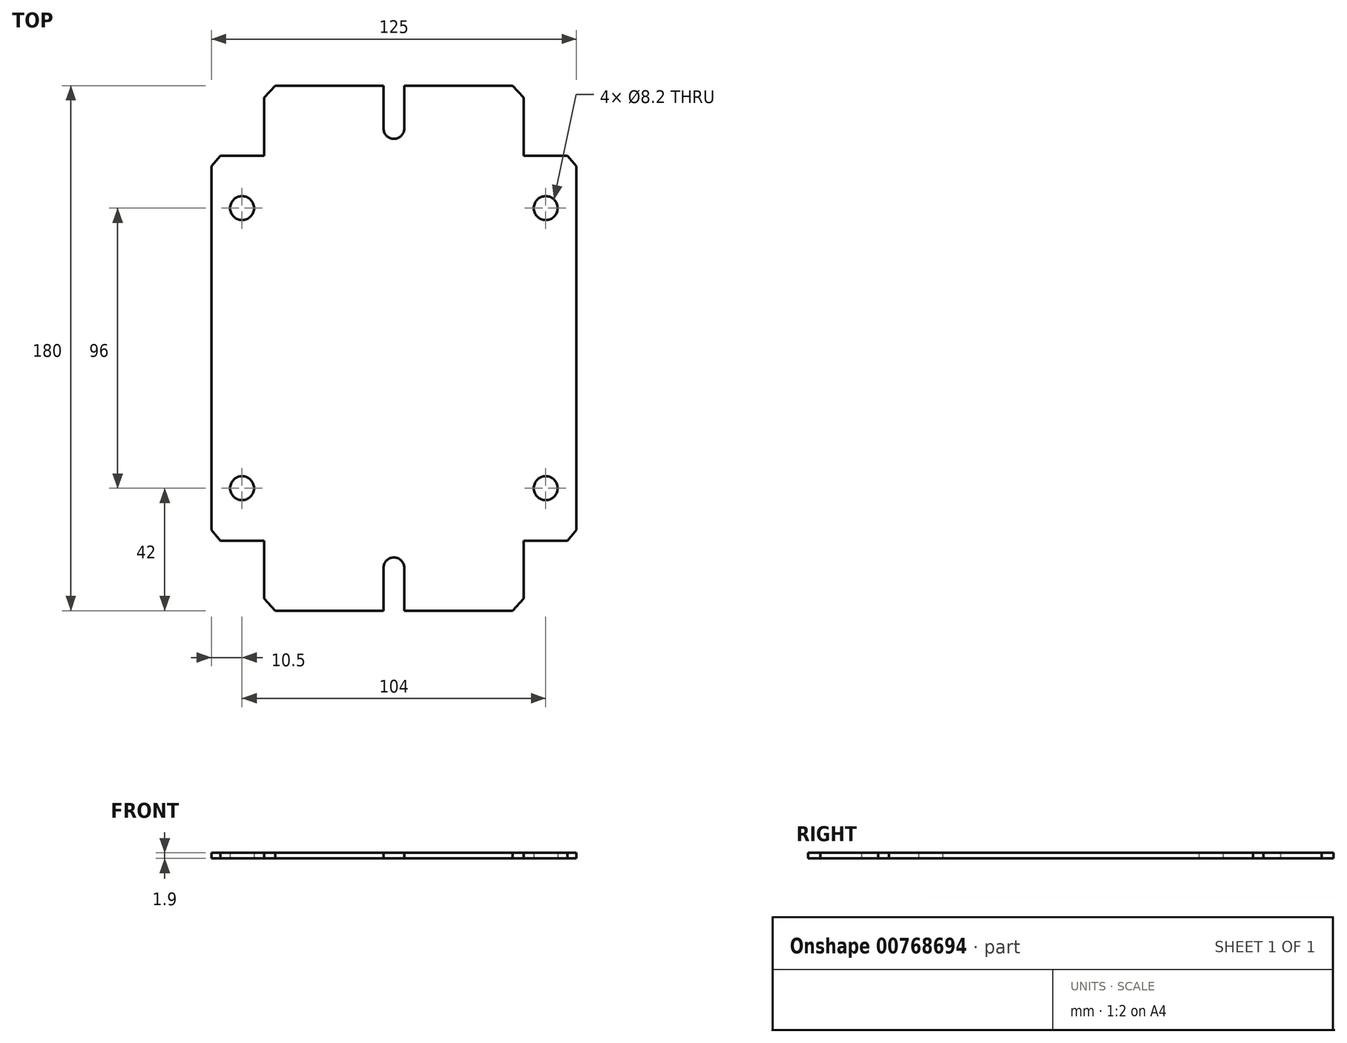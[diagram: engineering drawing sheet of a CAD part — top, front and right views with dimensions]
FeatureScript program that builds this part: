
annotation { "Feature Type Name" : "Feature", "Feature Type Description" : "" }
export const myFeature = defineFeature(function(context is Context, id is Id, definition is map)
    precondition{}
    {
        {
            var Q0;
            Q0=qCreatedBy(makeId("Top.planeOp"),FACE);
            var sketch = newSketch(context, id + "F0", { "sketchPlane" : qUnion([Q0])});
            skLineSegment(sketch, "E0.bottom", {"start": v(62.5, -90) * mm, "end": v(-62.5, -90) * mm});
            skLineSegment(sketch, "E0.top", {"start": v(62.5, 90) * mm, "end": v(-62.5, 90) * mm});
            skLineSegment(sketch, "E0.left", {"start": v(62.5, -90) * mm, "end": v(62.5, 90) * mm});
            skLineSegment(sketch, "E0.right", {"start": v(-62.5, -90) * mm, "end": v(-62.5, 90) * mm});
            skPoint(sketch, "E0.middle", {"position": v(0, 0) * mm});
            skLineSegment(sketch, "E1.bottom", {"start": v(-62.5, 90) * mm, "end": v(-44.5, 90) * mm});
            skLineSegment(sketch, "E1.top", {"start": v(-62.5, 66) * mm, "end": v(-44.5, 66) * mm});
            skLineSegment(sketch, "E1.left", {"start": v(-62.5, 90) * mm, "end": v(-62.5, 66) * mm});
            skLineSegment(sketch, "E1.right", {"start": v(-44.5, 90) * mm, "end": v(-44.5, 66) * mm});
            skLineSegment(sketch, "E2", {"start": v(-59.42, 66) * mm, "end": v(-62.5, 62.36) * mm});
            skCircle(sketch, "E3", {"center": v(-52, 48) * mm, "radius": 4.1 * mm});
            skLineSegment(sketch, "E4.MirrorCS", {"start": v(59.42, 66) * mm, "end": v(62.5, 62.36) * mm});
            skLineSegment(sketch, "E5.MirrorCS", {"start": v(44.5, 90) * mm, "end": v(44.5, 66) * mm});
            skLineSegment(sketch, "E6.MirrorCS", {"start": v(62.5, 90) * mm, "end": v(62.5, 66) * mm});
            skLineSegment(sketch, "E7.MirrorCS", {"start": v(62.5, 90) * mm, "end": v(44.5, 90) * mm});
            skLineSegment(sketch, "E8.MirrorCS", {"start": v(62.5, 66) * mm, "end": v(44.5, 66) * mm});
            skCircle(sketch, "E9.MirrorC", {"center": v(52, 48) * mm, "radius": 4.1 * mm});
            skCircle(sketch, "E10", {"center": v(0, 75.3) * mm, "radius": 3.55 * mm});
            skLineSegment(sketch, "E11", {"start": v(3.55, 75.3) * mm, "end": v(3.55, 90) * mm});
            skLineSegment(sketch, "E12", {"start": v(-3.55, 75.3) * mm, "end": v(-3.55, 90) * mm});
            skLineSegment(sketch, "E13.MirrorCS", {"start": v(-59.42, -66) * mm, "end": v(-62.5, -62.36) * mm});
            skLineSegment(sketch, "E14.MirrorCS", {"start": v(59.42, -66) * mm, "end": v(62.5, -62.36) * mm});
            skLineSegment(sketch, "E15.MirrorCS", {"start": v(62.5, -90) * mm, "end": v(44.5, -90) * mm});
            skCircle(sketch, "E16.MirrorC", {"center": v(0, -75.3) * mm, "radius": 3.55 * mm});
            skLineSegment(sketch, "E17.MirrorCS", {"start": v(-3.55, -75.3) * mm, "end": v(-3.55, -90) * mm});
            skLineSegment(sketch, "E18.MirrorCS", {"start": v(62.5, -90) * mm, "end": v(62.5, -66) * mm});
            skLineSegment(sketch, "E19.MirrorCS", {"start": v(44.5, -90) * mm, "end": v(44.5, -66) * mm});
            skLineSegment(sketch, "E20.MirrorCS", {"start": v(-44.5, -90) * mm, "end": v(-44.5, -66) * mm});
            skCircle(sketch, "E21.MirrorC", {"center": v(52, -48) * mm, "radius": 4.1 * mm});
            skLineSegment(sketch, "E22.MirrorCS", {"start": v(-62.5, -90) * mm, "end": v(-62.5, -66) * mm});
            skLineSegment(sketch, "E23.MirrorCS", {"start": v(62.5, -66) * mm, "end": v(44.5, -66) * mm});
            skLineSegment(sketch, "E24.MirrorCS", {"start": v(-62.5, -66) * mm, "end": v(-44.5, -66) * mm});
            skLineSegment(sketch, "E25.MirrorCS", {"start": v(-62.5, -90) * mm, "end": v(-44.5, -90) * mm});
            skCircle(sketch, "E26.MirrorC", {"center": v(-52, -48) * mm, "radius": 4.1 * mm});
            skLineSegment(sketch, "E27.MirrorCS", {"start": v(3.55, -75.3) * mm, "end": v(3.55, -90) * mm});
            skLineSegment(sketch, "E28", {"start": v(-44.5, 85.86) * mm, "end": v(-40.61, 90) * mm});
            skLineSegment(sketch, "E29.MirrorCS", {"start": v(44.5, 85.86) * mm, "end": v(40.61, 90) * mm});
            skLineSegment(sketch, "E30.MirrorCS", {"start": v(-44.5, -85.86) * mm, "end": v(-40.61, -90) * mm});
            skLineSegment(sketch, "E31.MirrorCS", {"start": v(44.5, -85.86) * mm, "end": v(40.61, -90) * mm});
            skSolve(sketch);
        }
        {
            var Q0;
            {var subQ16=sQuery(id+"F0.wireOp",EDGE,"E2");Q0=makeQuery(id+"F0.imprint","IMPRINT",FACE,{"disambiguationData":[TD([[makeQuery(id+"F0.imprint","IMPRINT",EDGE,{"derivedFrom":subQ16}),1.0]])]});}
            extrude(context, id + "F1", {"entities" : qUnion([Q0]), "depth" : 1.9 * mm, "offsetDistance" : 25 * mm});
        }
    });
